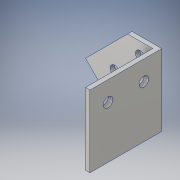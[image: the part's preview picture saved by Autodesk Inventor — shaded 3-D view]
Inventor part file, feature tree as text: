
AUTODESK INVENTOR PART (.ipt)
format: ipt  version: 2016 (Build 200138000, 138)  size: 109,056 bytes
history: native  units: in
note: dims shown in document units (in); Inventor stores cm internally (conversion verified against a paired STEP export)
features: sketch x4, other x3
ambient origin geometry x8: Origin, YZ Plane, XZ Plane, XY Plane, X Axis, Y Axis, Z Axis, Center Point
bodies: Solid1 (feature_tree)
feature tree (7):
  other  "bottom left rail gusset.ipt"
  other  "Solid1::bottom left rail gusset.ipt"
  other  "TaggingFeature1"
  sketch  "Sketch1"  dims[d0=0.3937in]
  sketch  "Sketch2"
  sketch  "Sketch3"
  sketch  "Sketch4"
